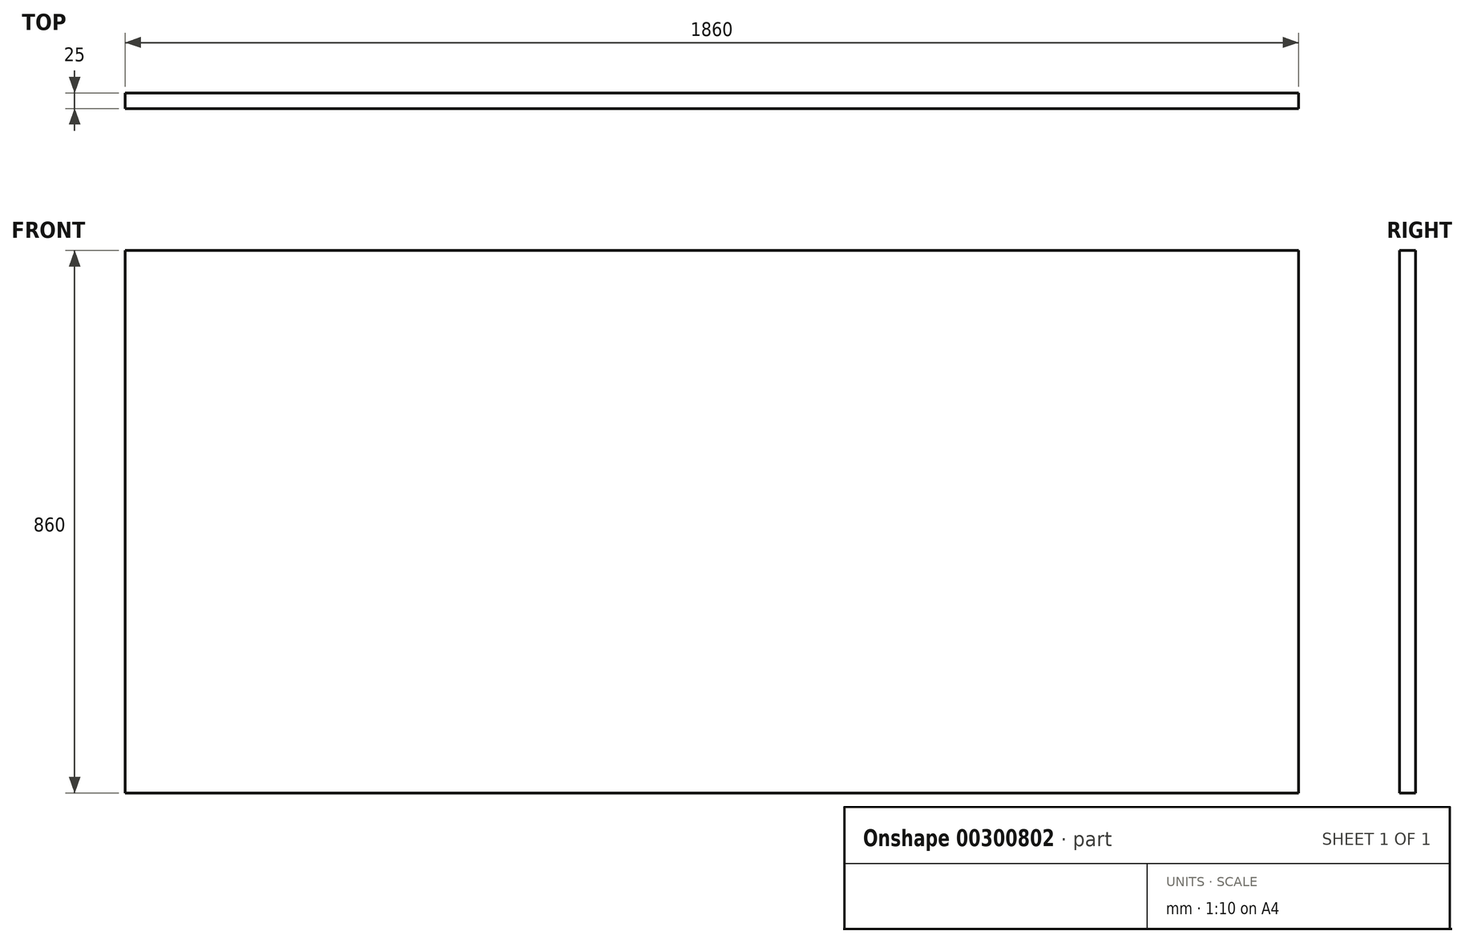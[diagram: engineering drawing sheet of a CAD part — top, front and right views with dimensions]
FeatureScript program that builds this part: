
annotation { "Feature Type Name" : "Feature", "Feature Type Description" : "" }
export const myFeature = defineFeature(function(context is Context, id is Id, definition is map)
    precondition{}
    {
        {
            var Q0;
            Q0=qCreatedBy(makeId("Front.planeOp"),FACE);
            var sketch = newSketch(context, id + "F0", { "sketchPlane" : qUnion([Q0])});
            skLineSegment(sketch, "E0.bottom", {"start": v(0, 0) * mm, "end": v(1860, 0) * mm});
            skLineSegment(sketch, "E0.top", {"start": v(0, -860) * mm, "end": v(1860, -860) * mm});
            skLineSegment(sketch, "E0.left", {"start": v(0, 0) * mm, "end": v(0, -860) * mm});
            skLineSegment(sketch, "E0.right", {"start": v(1860, 0) * mm, "end": v(1860, -860) * mm});
            skSolve(sketch);
        }
        {
            var Q0;
            Q0=makeQuery(id+"F0.imprint","IMPRINT",FACE,{"disambiguationData":[TD([[makeQuery(id+"F0.imprint","IMPRINT",EDGE,{"derivedFrom":sQuery(id+"F0.wireOp",EDGE,"E0.bottom")}),-1.0]])]});
            extrude(context, id + "F1", {"entities" : qUnion([Q0]), "depth" : 25 * mm});
        }
    });
